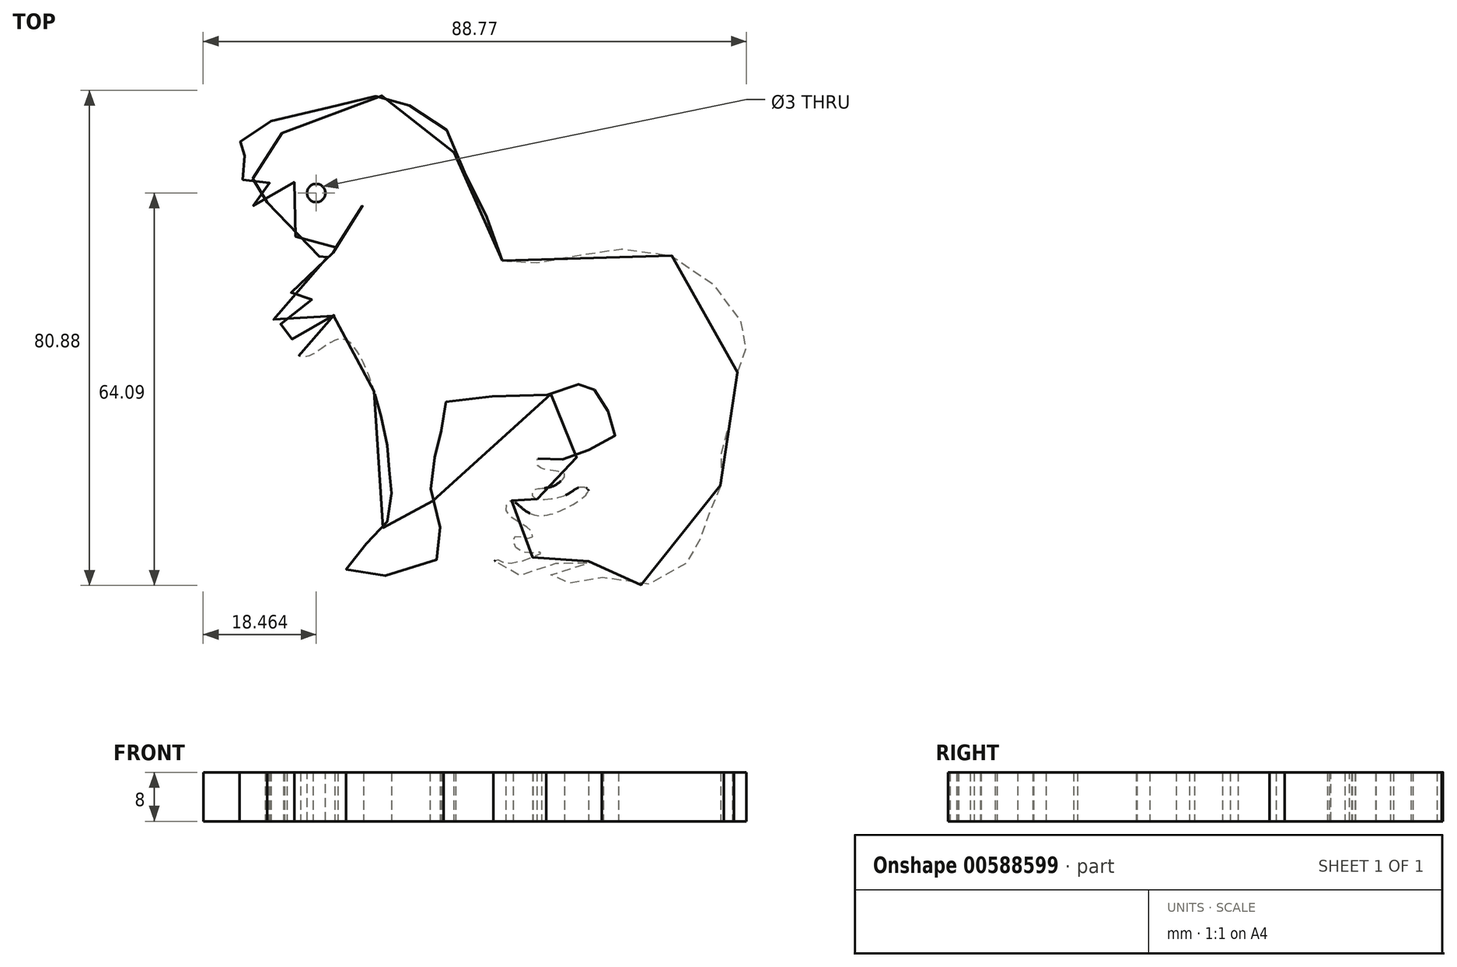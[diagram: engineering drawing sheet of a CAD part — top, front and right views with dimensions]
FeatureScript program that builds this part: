
annotation { "Feature Type Name" : "Feature", "Feature Type Description" : "" }
export const myFeature = defineFeature(function(context is Context, id is Id, definition is map)
    precondition{}
    {
        {
            var Q0;
            Q0=qCreatedBy(makeId("Top.planeOp"),FACE);
            var sketch = newSketch(context, id + "F0", { "sketchPlane" : qUnion([Q0])});
            skFitSpline(sketch, "E0", {"points": [v(-48, 53.72) * mm, v(-44.43, 53.33) * mm, v(-38.38, 53.8) * mm, v(-32.71, 55.5) * mm, v(-23.87, 55.2) * mm, v(-16.34, 52.64) * mm, v(-9.75, 44.8) * mm, v(-8.5, 42.7) * mm, v(-8.2, 39.53) * mm, v(-9.13, 37.66) * mm, v(-9.6, 35.57) * mm, v(-10.37, 33.78) * mm, v(-10.14, 31.61) * mm, v(-10.91, 28.43) * mm, v(-11.22, 24.24) * mm, v(-12.31, 22) * mm, v(-11.84, 18.43) * mm, v(-13.16, 15.7) * mm, v(-14.25, 12.37) * mm, v(-15.18, 10.59) * mm, v(-16.24, 6.63) * mm, v(-17.9, 4.66) * mm, v(-18.92, 2.27) * mm, v(-31.72, 1.4) * mm, v(-31.48, 2.4) * mm, v(-37.88, 1.04) * mm, v(-40.84, 2.15) * mm, v(-36.53, 3) * mm, v(-33.94, 4.73) * mm, v(-39.36, 4.24) * mm, v(-43.67, 2.52) * mm, v(-49.33, 3.38) * mm, v(-48.96, 4.98) * mm, v(-47.36, 4.36) * mm, v(-41.57, 6.09) * mm, v(-45.15, 6.33) * mm, v(-46, 8.67) * mm, v(-43.42, 8.43) * mm, v(-43.18, 9.53) * mm, v(-47.24, 12.61) * mm, v(-46.75, 14.58) * mm, v(-44.16, 12.86) * mm, v(-39.24, 12.61) * mm, v(-33.94, 16.3) * mm, v(-35.54, 16.68) * mm, v(-37.63, 15.45) * mm, v(-42.8, 15.08) * mm, v(-42.8, 16.3) * mm, v(-40.1, 16.8) * mm, v(-37.88, 18.9) * mm, v(-42.07, 20.13) * mm, v(-41.82, 21.73) * mm, v(-37.26, 21.23) * mm, v(-32.59, 23.7) * mm, v(-29.01, 26.16) * mm, v(-32.7, 31.7) * mm, v(-33.08, 32.93) * mm, v(-34.93, 33.67) * mm, v(-41.45, 31.7) * mm, v(-57.46, 30.47) * mm, v(-57.95, 24.8) * mm, v(-59.55, 20.37) * mm, v(-58.7, 11.87) * mm, v(-58.81, 4.86) * mm, v(-73.35, 3) * mm, v(-69.77, 7.93) * mm, v(-66.45, 12) * mm, v(-66.2, 17.3) * mm, v(-66.57, 20.25) * mm, v(-66.94, 24.56) * mm, v(-68.17, 29.6) * mm, v(-69.16, 33.06) * mm, v(-73.96, 40.94) * mm, v(-79.87, 38.1) * mm, v(-81.97, 38.72) * mm, v(-79.87, 40.32) * mm, v(-75.44, 45.37) * mm, v(-78.89, 44.26) * mm, v(-82.34, 40.94) * mm, v(-86.4, 40.44) * mm, v(-83.57, 42.9) * mm, v(-86.15, 43.9) * mm, v(-81.23, 45.37) * mm, v(-79.01, 48.08) * mm, v(-81.84, 46.85) * mm, v(-83.2, 48.08) * mm, v(-80.73, 49.19) * mm, v(-77.78, 53) * mm, v(-74.2, 56.08) * mm, v(-71.38, 58.8) * mm, v(-71.13, 62.98) * mm, v(-74.7, 59.16) * mm, v(-75.07, 56.08) * mm, v(-79.26, 54.36) * mm, v(-81.97, 56.45) * mm, v(-80.98, 59.9) * mm, v(-81.6, 62.24) * mm, v(-82.21, 67.17) * mm, v(-83.94, 65.44) * mm, v(-88.25, 62.73) * mm, v(-90.96, 63.47) * mm, v(-88.86, 64.21) * mm, v(-85.9, 66.67) * mm, v(-88.86, 65.56) * mm, v(-90.96, 67.29) * mm, v(-89.48, 66.8) * mm, v(-86.77, 70.37) * mm, v(-88.37, 70.61) * mm, v(-96.87, 73.32) * mm, v(-85.78, 73.08) * mm, v(-83.81, 74.3) * mm, v(-85.78, 76.52) * mm, v(-80.24, 76.4) * mm, v(-76.42, 78.62) * mm, v(-72.73, 81.57) * mm, v(-70.4, 80.83) * mm, v(-66.57, 80.96) * mm, v(-65.34, 81.33) * mm, v(-64.36, 79.48) * mm, v(-61.9, 78.99) * mm, v(-59.43, 77.14) * mm, v(-57.7, 75.3) * mm, v(-55.74, 74.3) * mm, v(-55.86, 70.12) * mm, v(-53.64, 67.54) * mm, v(-52.78, 63.35) * mm, v(-50.69, 61.13) * mm, v(-50.32, 59.78) * mm, v(-49.2, 57.44) * mm, v(-48, 53.72) * mm]});
            skSolve(sketch);
        }
        {
            var Q0;
            Q0 = qSketchRegion(id + "F0", true);
            extrude(context, id + "F1", {"entities" : qUnion([Q0]), "depth" : 8 * mm, "offsetDistance" : 25 * mm});
        }
        {
            var Q0;
            Q0=makeQuery(id+"F1.opExtrude","CAP_FACE",FACE,{"disambiguationData":[OSD([sQuery(id+"F0.wireOp",EDGE,"E0")])],"isStart":false});
            var sketch = newSketch(context, id + "F2", { "sketchPlane" : qUnion([Q0])});
            skPoint(sketch, "E1", {"position": v(-78.4, 64.92) * mm});
            skPoint(sketch, "E2", {"position": v(-78.4, 64.8) * mm});
            skSolve(sketch);
        }
        {
            var Q0;
            Q0=sQuery(id+"F2.wireOp",VERTEX,"E2");
            var Q1;
            Q1=makeQuery(id+"F1.opExtrude","SWEPT_BODY",BODY,{"disambiguationData":[OSD([sQuery(id+"F0.wireOp",EDGE,"E0")])]});
            hole(context, id + "F3", {"style" : HoleStyle.SIMPLE, "endStyle" : HoleEndStyle.THROUGH, "holeDiameter" : 3 * mm, "majorDiameter" : 5 * mm, "isTappedThrough" : true, "tappedDepth" : 12 * mm, "tapClearance" : 3, "locations" : qUnion([Q0]), "scope" : qUnion([Q1])});
        }
    });
